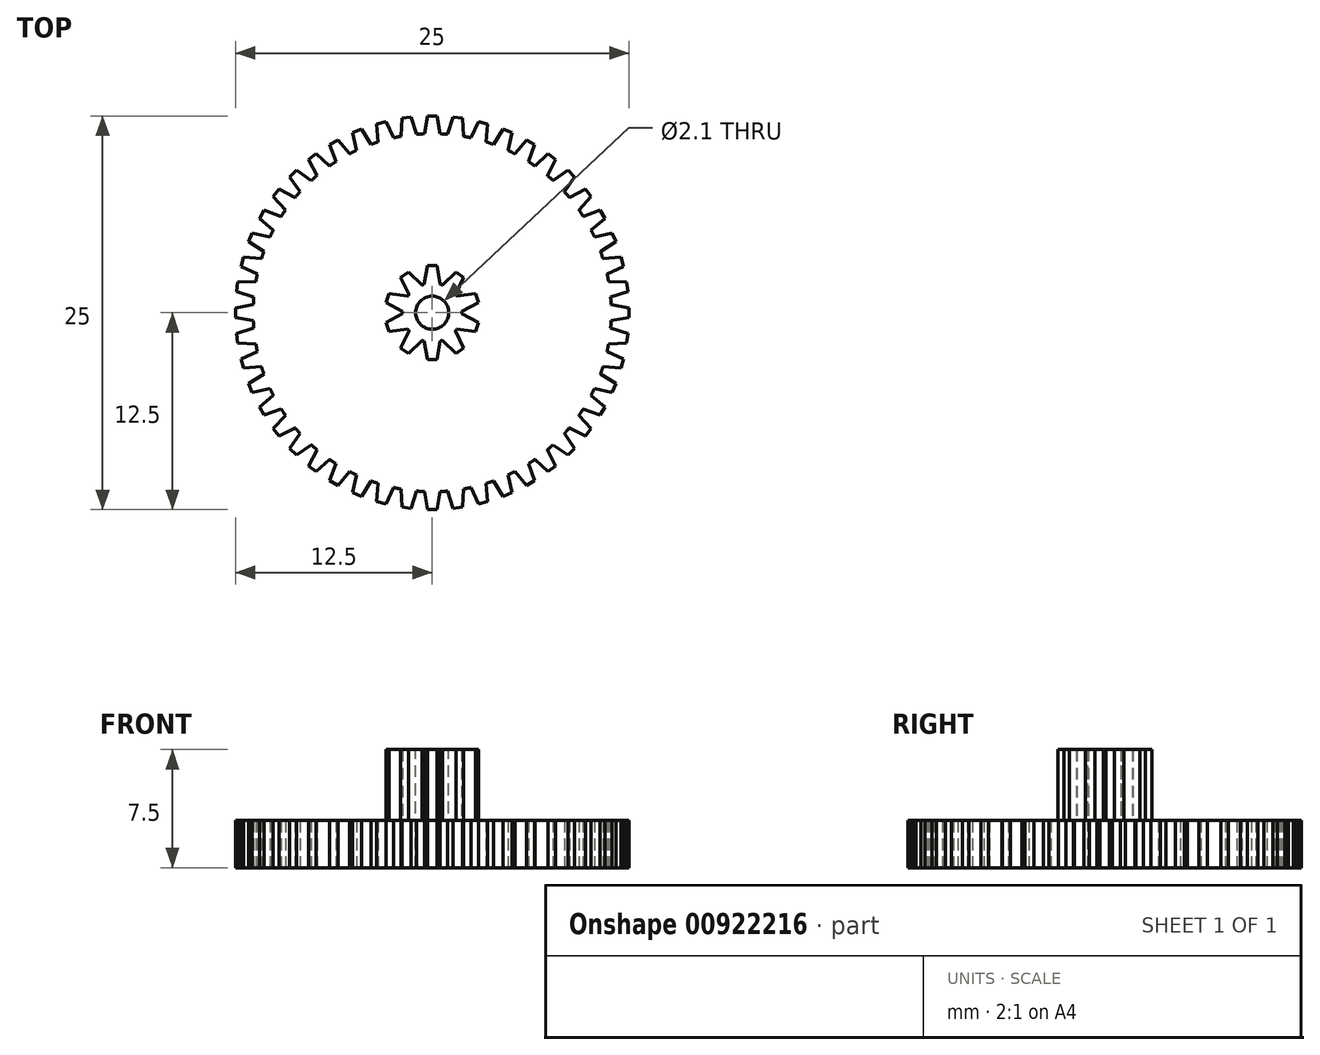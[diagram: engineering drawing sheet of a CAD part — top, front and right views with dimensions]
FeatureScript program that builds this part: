
annotation { "Feature Type Name" : "Feature", "Feature Type Description" : "" }
export const myFeature = defineFeature(function(context is Context, id is Id, definition is map)
    precondition{}
    {
        {
            var Q0;
            Q0=qCreatedBy(makeId("Top.planeOp"),FACE);
            var sketch = newSketch(context, id + "F0", { "sketchPlane" : qUnion([Q0])});
            skCircle(sketch, "E0", {"center": v(0, 0) * mm, "radius": 12 * mm, "construction": true});
            skCircle(sketch, "E1", {"center": v(0, 0) * mm, "radius": 12.5 * mm, "construction": true});
            skCircle(sketch, "E2", {"center": v(0, 0) * mm, "radius": 11.38 * mm});
            skLineSegment(sketch, "E3", {"start": v(0, 11.38) * mm, "end": v(0.5, 11.38) * mm, "construction": true});
            skLineSegment(sketch, "E4", {"start": v(0, 11.38) * mm, "end": v(-0.5, 11.38) * mm, "construction": true});
            skLineSegment(sketch, "E5", {"start": v(-1.28, 6.98) * mm, "end": v(-0.5, 11.36) * mm, "construction": true});
            skLineSegment(sketch, "E6", {"start": v(1.27, 6.98) * mm, "end": v(0.3, 12.5) * mm, "construction": true});
            skLineSegment(sketch, "E7", {"start": v(-1.27, 6.99) * mm, "end": v(-0.3, 12.5) * mm});
            skLineSegment(sketch, "E8", {"start": v(0.3, 12.5) * mm, "end": v(-0.3, 12.5) * mm});
            skLineSegment(sketch, "E9", {"start": v(0.3, 12.5) * mm, "end": v(0.5, 11.36) * mm});
            skLineSegment(sketch, "E10.1.0", {"start": v(-2.17, 6.76) * mm, "end": v(-1.93, 12.35) * mm});
            skLineSegment(sketch, "E10.1.1", {"start": v(-1.33, 12.43) * mm, "end": v(-1.93, 12.35) * mm});
            skLineSegment(sketch, "E10.1.2", {"start": v(-1.33, 12.43) * mm, "end": v(-0.99, 11.33) * mm});
            skLineSegment(sketch, "E10.2.0", {"start": v(-3.04, 6.42) * mm, "end": v(-3.53, 12) * mm});
            skLineSegment(sketch, "E10.2.1", {"start": v(-2.94, 12.15) * mm, "end": v(-3.53, 12) * mm});
            skLineSegment(sketch, "E10.2.2", {"start": v(-2.94, 12.15) * mm, "end": v(-2.46, 11.1) * mm});
            skLineSegment(sketch, "E11.1.3.0", {"start": v(-3.85, 5.97) * mm, "end": v(-5.06, 11.43) * mm});
            skLineSegment(sketch, "E11.3.3.0", {"start": v(-4.5, 11.66) * mm, "end": v(-5.06, 11.43) * mm});
            skLineSegment(sketch, "E11.6.3.0", {"start": v(-4.5, 11.66) * mm, "end": v(-3.89, 10.7) * mm});
            skLineSegment(sketch, "E11.1.4.0", {"start": v(-4.6, 5.42) * mm, "end": v(-6.5, 10.67) * mm});
            skLineSegment(sketch, "E11.3.4.0", {"start": v(-5.99, 10.97) * mm, "end": v(-6.5, 10.67) * mm});
            skLineSegment(sketch, "E11.6.4.0", {"start": v(-5.99, 10.97) * mm, "end": v(-5.25, 10.1) * mm});
            skLineSegment(sketch, "E11.1.5.0", {"start": v(-5.26, 4.77) * mm, "end": v(-7.85, 9.73) * mm});
            skLineSegment(sketch, "E11.3.5.0", {"start": v(-7.37, 10.1) * mm, "end": v(-7.85, 9.73) * mm});
            skLineSegment(sketch, "E11.6.5.0", {"start": v(-7.37, 10.1) * mm, "end": v(-6.52, 9.32) * mm});
            skLineSegment(sketch, "E11.1.6.0", {"start": v(-5.84, 4.04) * mm, "end": v(-9.05, 8.62) * mm});
            skLineSegment(sketch, "E11.3.6.0", {"start": v(-8.62, 9.05) * mm, "end": v(-9.05, 8.62) * mm});
            skLineSegment(sketch, "E11.6.6.0", {"start": v(-8.62, 9.05) * mm, "end": v(-7.68, 8.4) * mm});
            skLineSegment(sketch, "E11.1.7.0", {"start": v(-6.32, 3.24) * mm, "end": v(-10.1, 7.37) * mm});
            skLineSegment(sketch, "E11.3.7.0", {"start": v(-9.73, 7.85) * mm, "end": v(-10.1, 7.37) * mm});
            skLineSegment(sketch, "E11.6.7.0", {"start": v(-9.73, 7.85) * mm, "end": v(-8.71, 7.32) * mm});
            skLineSegment(sketch, "E11.1.8.0", {"start": v(-6.69, 2.4) * mm, "end": v(-10.97, 5.99) * mm});
            skLineSegment(sketch, "E11.3.8.0", {"start": v(-10.67, 6.5) * mm, "end": v(-10.97, 5.99) * mm});
            skLineSegment(sketch, "E11.6.8.0", {"start": v(-10.67, 6.5) * mm, "end": v(-9.6, 6.12) * mm});
            skLineSegment(sketch, "E11.1.9.0", {"start": v(-6.94, 1.5) * mm, "end": v(-11.66, 4.5) * mm});
            skLineSegment(sketch, "E11.3.9.0", {"start": v(-11.43, 5.06) * mm, "end": v(-11.66, 4.5) * mm});
            skLineSegment(sketch, "E11.6.9.0", {"start": v(-11.43, 5.06) * mm, "end": v(-10.3, 4.81) * mm});
            skLineSegment(sketch, "E11.1.10.0", {"start": v(-7.08, 0.58) * mm, "end": v(-12.15, 2.94) * mm});
            skLineSegment(sketch, "E11.3.10.0", {"start": v(-12, 3.53) * mm, "end": v(-12.15, 2.94) * mm});
            skLineSegment(sketch, "E11.6.10.0", {"start": v(-12, 3.53) * mm, "end": v(-10.85, 3.43) * mm});
            skLineSegment(sketch, "E11.1.11.0", {"start": v(-7.1, -0.35) * mm, "end": v(-12.43, 1.33) * mm});
            skLineSegment(sketch, "E11.3.11.0", {"start": v(-12.35, 1.93) * mm, "end": v(-12.43, 1.33) * mm});
            skLineSegment(sketch, "E11.6.11.0", {"start": v(-12.35, 1.93) * mm, "end": v(-11.2, 1.98) * mm});
            skLineSegment(sketch, "E11.1.12.0", {"start": v(-6.99, -1.27) * mm, "end": v(-12.5, -0.3) * mm});
            skLineSegment(sketch, "E11.3.12.0", {"start": v(-12.5, 0.3) * mm, "end": v(-12.5, -0.3) * mm});
            skLineSegment(sketch, "E11.6.12.0", {"start": v(-12.5, 0.3) * mm, "end": v(-11.36, 0.5) * mm});
            skLineSegment(sketch, "E11.1.13.0", {"start": v(-6.76, -2.17) * mm, "end": v(-12.35, -1.93) * mm});
            skLineSegment(sketch, "E11.3.13.0", {"start": v(-12.43, -1.33) * mm, "end": v(-12.35, -1.93) * mm});
            skLineSegment(sketch, "E11.6.13.0", {"start": v(-12.43, -1.33) * mm, "end": v(-11.33, -0.99) * mm});
            skLineSegment(sketch, "E11.1.14.0", {"start": v(-6.42, -3.04) * mm, "end": v(-12, -3.53) * mm});
            skLineSegment(sketch, "E11.3.14.0", {"start": v(-12.15, -2.94) * mm, "end": v(-12, -3.53) * mm});
            skLineSegment(sketch, "E11.6.14.0", {"start": v(-12.15, -2.94) * mm, "end": v(-11.1, -2.46) * mm});
            skLineSegment(sketch, "E11.1.15.0", {"start": v(-5.97, -3.85) * mm, "end": v(-11.43, -5.06) * mm});
            skLineSegment(sketch, "E11.3.15.0", {"start": v(-11.66, -4.5) * mm, "end": v(-11.43, -5.06) * mm});
            skLineSegment(sketch, "E11.6.15.0", {"start": v(-11.66, -4.5) * mm, "end": v(-10.7, -3.89) * mm});
            skLineSegment(sketch, "E11.1.16.0", {"start": v(-5.42, -4.6) * mm, "end": v(-10.67, -6.5) * mm});
            skLineSegment(sketch, "E11.3.16.0", {"start": v(-10.97, -5.99) * mm, "end": v(-10.67, -6.5) * mm});
            skLineSegment(sketch, "E11.6.16.0", {"start": v(-10.97, -5.99) * mm, "end": v(-10.1, -5.25) * mm});
            skLineSegment(sketch, "E11.1.17.0", {"start": v(-4.77, -5.26) * mm, "end": v(-9.73, -7.85) * mm});
            skLineSegment(sketch, "E11.3.17.0", {"start": v(-10.1, -7.37) * mm, "end": v(-9.73, -7.85) * mm});
            skLineSegment(sketch, "E11.6.17.0", {"start": v(-10.1, -7.37) * mm, "end": v(-9.32, -6.52) * mm});
            skLineSegment(sketch, "E11.1.18.0", {"start": v(-4.04, -5.84) * mm, "end": v(-8.62, -9.05) * mm});
            skLineSegment(sketch, "E11.3.18.0", {"start": v(-9.05, -8.62) * mm, "end": v(-8.62, -9.05) * mm});
            skLineSegment(sketch, "E11.6.18.0", {"start": v(-9.05, -8.62) * mm, "end": v(-8.4, -7.68) * mm});
            skLineSegment(sketch, "E11.1.19.0", {"start": v(-3.24, -6.32) * mm, "end": v(-7.37, -10.1) * mm});
            skLineSegment(sketch, "E11.3.19.0", {"start": v(-7.85, -9.73) * mm, "end": v(-7.37, -10.1) * mm});
            skLineSegment(sketch, "E11.6.19.0", {"start": v(-7.85, -9.73) * mm, "end": v(-7.32, -8.71) * mm});
            skLineSegment(sketch, "E11.1.20.0", {"start": v(-2.4, -6.69) * mm, "end": v(-5.99, -10.97) * mm});
            skLineSegment(sketch, "E11.3.20.0", {"start": v(-6.5, -10.67) * mm, "end": v(-5.99, -10.97) * mm});
            skLineSegment(sketch, "E11.6.20.0", {"start": v(-6.5, -10.67) * mm, "end": v(-6.12, -9.6) * mm});
            skLineSegment(sketch, "E11.1.21.0", {"start": v(-1.5, -6.94) * mm, "end": v(-4.5, -11.66) * mm});
            skLineSegment(sketch, "E11.3.21.0", {"start": v(-5.06, -11.43) * mm, "end": v(-4.5, -11.66) * mm});
            skLineSegment(sketch, "E11.6.21.0", {"start": v(-5.06, -11.43) * mm, "end": v(-4.81, -10.3) * mm});
            skLineSegment(sketch, "E11.1.22.0", {"start": v(-0.58, -7.08) * mm, "end": v(-2.94, -12.15) * mm});
            skLineSegment(sketch, "E11.3.22.0", {"start": v(-3.53, -12) * mm, "end": v(-2.94, -12.15) * mm});
            skLineSegment(sketch, "E11.6.22.0", {"start": v(-3.53, -12) * mm, "end": v(-3.43, -10.85) * mm});
            skLineSegment(sketch, "E11.1.23.0", {"start": v(0.35, -7.1) * mm, "end": v(-1.33, -12.43) * mm});
            skLineSegment(sketch, "E11.3.23.0", {"start": v(-1.93, -12.35) * mm, "end": v(-1.33, -12.43) * mm});
            skLineSegment(sketch, "E11.6.23.0", {"start": v(-1.93, -12.35) * mm, "end": v(-1.98, -11.2) * mm});
            skLineSegment(sketch, "E11.1.24.0", {"start": v(1.27, -6.99) * mm, "end": v(0.3, -12.5) * mm});
            skLineSegment(sketch, "E11.3.24.0", {"start": v(-0.3, -12.5) * mm, "end": v(0.3, -12.5) * mm});
            skLineSegment(sketch, "E11.6.24.0", {"start": v(-0.3, -12.5) * mm, "end": v(-0.5, -11.36) * mm});
            skLineSegment(sketch, "E11.1.25.0", {"start": v(2.17, -6.76) * mm, "end": v(1.93, -12.35) * mm});
            skLineSegment(sketch, "E11.3.25.0", {"start": v(1.33, -12.43) * mm, "end": v(1.93, -12.35) * mm});
            skLineSegment(sketch, "E11.6.25.0", {"start": v(1.33, -12.43) * mm, "end": v(0.99, -11.33) * mm});
            skLineSegment(sketch, "E11.1.26.0", {"start": v(3.04, -6.42) * mm, "end": v(3.53, -12) * mm});
            skLineSegment(sketch, "E11.3.26.0", {"start": v(2.94, -12.15) * mm, "end": v(3.53, -12) * mm});
            skLineSegment(sketch, "E11.6.26.0", {"start": v(2.94, -12.15) * mm, "end": v(2.46, -11.1) * mm});
            skLineSegment(sketch, "E11.1.27.0", {"start": v(3.85, -5.97) * mm, "end": v(5.06, -11.43) * mm});
            skLineSegment(sketch, "E11.3.27.0", {"start": v(4.5, -11.66) * mm, "end": v(5.06, -11.43) * mm});
            skLineSegment(sketch, "E11.6.27.0", {"start": v(4.5, -11.66) * mm, "end": v(3.89, -10.7) * mm});
            skLineSegment(sketch, "E11.1.28.0", {"start": v(4.6, -5.42) * mm, "end": v(6.5, -10.67) * mm});
            skLineSegment(sketch, "E11.3.28.0", {"start": v(5.99, -10.97) * mm, "end": v(6.5, -10.67) * mm});
            skLineSegment(sketch, "E11.6.28.0", {"start": v(5.99, -10.97) * mm, "end": v(5.25, -10.1) * mm});
            skLineSegment(sketch, "E11.1.29.0", {"start": v(5.26, -4.77) * mm, "end": v(7.85, -9.73) * mm});
            skLineSegment(sketch, "E11.3.29.0", {"start": v(7.37, -10.1) * mm, "end": v(7.85, -9.73) * mm});
            skLineSegment(sketch, "E11.6.29.0", {"start": v(7.37, -10.1) * mm, "end": v(6.52, -9.32) * mm});
            skLineSegment(sketch, "E12.1.30.0", {"start": v(5.84, -4.04) * mm, "end": v(9.05, -8.62) * mm});
            skLineSegment(sketch, "E12.3.30.0", {"start": v(8.62, -9.05) * mm, "end": v(9.05, -8.62) * mm});
            skLineSegment(sketch, "E12.6.30.0", {"start": v(8.62, -9.05) * mm, "end": v(7.68, -8.4) * mm});
            skLineSegment(sketch, "E12.1.31.0", {"start": v(6.32, -3.24) * mm, "end": v(10.1, -7.37) * mm});
            skLineSegment(sketch, "E12.3.31.0", {"start": v(9.73, -7.85) * mm, "end": v(10.1, -7.37) * mm});
            skLineSegment(sketch, "E12.6.31.0", {"start": v(9.73, -7.85) * mm, "end": v(8.71, -7.32) * mm});
            skLineSegment(sketch, "E12.1.32.0", {"start": v(6.69, -2.4) * mm, "end": v(10.97, -5.99) * mm});
            skLineSegment(sketch, "E12.3.32.0", {"start": v(10.67, -6.5) * mm, "end": v(10.97, -5.99) * mm});
            skLineSegment(sketch, "E12.6.32.0", {"start": v(10.67, -6.5) * mm, "end": v(9.6, -6.12) * mm});
            skLineSegment(sketch, "E12.1.33.0", {"start": v(6.94, -1.5) * mm, "end": v(11.66, -4.5) * mm});
            skLineSegment(sketch, "E12.3.33.0", {"start": v(11.43, -5.06) * mm, "end": v(11.66, -4.5) * mm});
            skLineSegment(sketch, "E12.6.33.0", {"start": v(11.43, -5.06) * mm, "end": v(10.3, -4.81) * mm});
            skLineSegment(sketch, "E12.1.34.0", {"start": v(7.08, -0.58) * mm, "end": v(12.15, -2.94) * mm});
            skLineSegment(sketch, "E12.3.34.0", {"start": v(12, -3.53) * mm, "end": v(12.15, -2.94) * mm});
            skLineSegment(sketch, "E12.6.34.0", {"start": v(12, -3.53) * mm, "end": v(10.85, -3.43) * mm});
            skLineSegment(sketch, "E12.1.35.0", {"start": v(7.1, 0.35) * mm, "end": v(12.43, -1.33) * mm});
            skLineSegment(sketch, "E12.3.35.0", {"start": v(12.35, -1.93) * mm, "end": v(12.43, -1.33) * mm});
            skLineSegment(sketch, "E12.6.35.0", {"start": v(12.35, -1.93) * mm, "end": v(11.2, -1.98) * mm});
            skLineSegment(sketch, "E12.1.36.0", {"start": v(6.99, 1.27) * mm, "end": v(12.5, 0.3) * mm});
            skLineSegment(sketch, "E12.3.36.0", {"start": v(12.5, -0.3) * mm, "end": v(12.5, 0.3) * mm});
            skLineSegment(sketch, "E12.6.36.0", {"start": v(12.5, -0.3) * mm, "end": v(11.36, -0.5) * mm});
            skLineSegment(sketch, "E12.1.37.0", {"start": v(6.76, 2.17) * mm, "end": v(12.35, 1.93) * mm});
            skLineSegment(sketch, "E12.3.37.0", {"start": v(12.43, 1.33) * mm, "end": v(12.35, 1.93) * mm});
            skLineSegment(sketch, "E12.6.37.0", {"start": v(12.43, 1.33) * mm, "end": v(11.33, 0.99) * mm});
            skLineSegment(sketch, "E12.1.38.0", {"start": v(6.42, 3.04) * mm, "end": v(12, 3.53) * mm});
            skLineSegment(sketch, "E12.3.38.0", {"start": v(12.15, 2.94) * mm, "end": v(12, 3.53) * mm});
            skLineSegment(sketch, "E12.6.38.0", {"start": v(12.15, 2.94) * mm, "end": v(11.1, 2.46) * mm});
            skLineSegment(sketch, "E12.1.39.0", {"start": v(5.97, 3.85) * mm, "end": v(11.43, 5.06) * mm});
            skLineSegment(sketch, "E12.3.39.0", {"start": v(11.66, 4.5) * mm, "end": v(11.43, 5.06) * mm});
            skLineSegment(sketch, "E12.6.39.0", {"start": v(11.66, 4.5) * mm, "end": v(10.7, 3.89) * mm});
            skLineSegment(sketch, "E12.1.40.0", {"start": v(5.42, 4.6) * mm, "end": v(10.67, 6.5) * mm});
            skLineSegment(sketch, "E12.3.40.0", {"start": v(10.97, 5.99) * mm, "end": v(10.67, 6.5) * mm});
            skLineSegment(sketch, "E12.6.40.0", {"start": v(10.97, 5.99) * mm, "end": v(10.1, 5.25) * mm});
            skLineSegment(sketch, "E12.1.41.0", {"start": v(4.77, 5.26) * mm, "end": v(9.73, 7.85) * mm});
            skLineSegment(sketch, "E12.3.41.0", {"start": v(10.1, 7.37) * mm, "end": v(9.73, 7.85) * mm});
            skLineSegment(sketch, "E12.6.41.0", {"start": v(10.1, 7.37) * mm, "end": v(9.32, 6.52) * mm});
            skLineSegment(sketch, "E13.1.42.0", {"start": v(4.04, 5.84) * mm, "end": v(8.62, 9.05) * mm});
            skLineSegment(sketch, "E13.3.42.0", {"start": v(9.05, 8.62) * mm, "end": v(8.62, 9.05) * mm});
            skLineSegment(sketch, "E13.6.42.0", {"start": v(9.05, 8.62) * mm, "end": v(8.4, 7.68) * mm});
            skLineSegment(sketch, "E13.1.43.0", {"start": v(3.24, 6.32) * mm, "end": v(7.37, 10.1) * mm});
            skLineSegment(sketch, "E13.3.43.0", {"start": v(7.85, 9.73) * mm, "end": v(7.37, 10.1) * mm});
            skLineSegment(sketch, "E13.6.43.0", {"start": v(7.85, 9.73) * mm, "end": v(7.32, 8.71) * mm});
            skLineSegment(sketch, "E13.1.44.0", {"start": v(2.4, 6.69) * mm, "end": v(5.99, 10.97) * mm});
            skLineSegment(sketch, "E13.3.44.0", {"start": v(6.5, 10.67) * mm, "end": v(5.99, 10.97) * mm});
            skLineSegment(sketch, "E13.6.44.0", {"start": v(6.5, 10.67) * mm, "end": v(6.12, 9.6) * mm});
            skLineSegment(sketch, "E13.1.45.0", {"start": v(1.5, 6.94) * mm, "end": v(4.5, 11.66) * mm});
            skLineSegment(sketch, "E13.3.45.0", {"start": v(5.06, 11.43) * mm, "end": v(4.5, 11.66) * mm});
            skLineSegment(sketch, "E13.6.45.0", {"start": v(5.06, 11.43) * mm, "end": v(4.81, 10.3) * mm});
            skLineSegment(sketch, "E13.1.46.0", {"start": v(0.58, 7.08) * mm, "end": v(2.94, 12.15) * mm});
            skLineSegment(sketch, "E13.3.46.0", {"start": v(3.53, 12) * mm, "end": v(2.94, 12.15) * mm});
            skLineSegment(sketch, "E13.6.46.0", {"start": v(3.53, 12) * mm, "end": v(3.43, 10.85) * mm});
            skLineSegment(sketch, "E13.1.47.0", {"start": v(-0.35, 7.1) * mm, "end": v(1.33, 12.43) * mm});
            skLineSegment(sketch, "E13.3.47.0", {"start": v(1.93, 12.35) * mm, "end": v(1.33, 12.43) * mm});
            skLineSegment(sketch, "E13.6.47.0", {"start": v(1.93, 12.35) * mm, "end": v(1.98, 11.2) * mm});
            skSolve(sketch);
        }
        {
            var Q0;
            Q0=qSketchRegion(id+"F0",true);
            extrude(context, id + "F1", {"entities" : qUnion([Q0]), "depth" : 3 * mm, "offsetDistance" : 25 * mm});
        }
        {
            var Q0;
            Q0=makeQuery(id+"F1.opExtrude","CAP_FACE",FACE,{"disambiguationData":[OSD([sQuery(id+"F0.wireOp",EDGE,"E2"),sQuery(id+"F0.wireOp",EDGE,"E7"),sQuery(id+"F0.wireOp",EDGE,"E8"),sQuery(id+"F0.wireOp",EDGE,"E9"),sQuery(id+"F0.wireOp",EDGE,"E10.1.0"),sQuery(id+"F0.wireOp",EDGE,"E10.1.1"),sQuery(id+"F0.wireOp",EDGE,"E10.1.2"),sQuery(id+"F0.wireOp",EDGE,"E10.2.0"),sQuery(id+"F0.wireOp",EDGE,"E10.2.1"),sQuery(id+"F0.wireOp",EDGE,"E10.2.2"),sQuery(id+"F0.wireOp",EDGE,"E11.1.3.0"),sQuery(id+"F0.wireOp",EDGE,"E11.3.3.0"),sQuery(id+"F0.wireOp",EDGE,"E11.6.3.0"),sQuery(id+"F0.wireOp",EDGE,"E11.1.4.0"),sQuery(id+"F0.wireOp",EDGE,"E11.3.4.0"),sQuery(id+"F0.wireOp",EDGE,"E11.6.4.0"),sQuery(id+"F0.wireOp",EDGE,"E11.1.5.0"),sQuery(id+"F0.wireOp",EDGE,"E11.3.5.0"),sQuery(id+"F0.wireOp",EDGE,"E11.6.5.0"),sQuery(id+"F0.wireOp",EDGE,"E11.1.6.0"),sQuery(id+"F0.wireOp",EDGE,"E11.3.6.0"),sQuery(id+"F0.wireOp",EDGE,"E11.6.6.0"),sQuery(id+"F0.wireOp",EDGE,"E11.1.7.0"),sQuery(id+"F0.wireOp",EDGE,"E11.3.7.0"),sQuery(id+"F0.wireOp",EDGE,"E11.6.7.0"),sQuery(id+"F0.wireOp",EDGE,"E11.1.8.0"),sQuery(id+"F0.wireOp",EDGE,"E11.3.8.0"),sQuery(id+"F0.wireOp",EDGE,"E11.6.8.0"),sQuery(id+"F0.wireOp",EDGE,"E11.1.9.0"),sQuery(id+"F0.wireOp",EDGE,"E11.3.9.0"),sQuery(id+"F0.wireOp",EDGE,"E11.6.9.0"),sQuery(id+"F0.wireOp",EDGE,"E11.1.10.0"),sQuery(id+"F0.wireOp",EDGE,"E11.3.10.0"),sQuery(id+"F0.wireOp",EDGE,"E11.6.10.0"),sQuery(id+"F0.wireOp",EDGE,"E11.1.11.0"),sQuery(id+"F0.wireOp",EDGE,"E11.3.11.0"),sQuery(id+"F0.wireOp",EDGE,"E11.6.11.0"),sQuery(id+"F0.wireOp",EDGE,"E11.1.12.0"),sQuery(id+"F0.wireOp",EDGE,"E11.3.12.0"),sQuery(id+"F0.wireOp",EDGE,"E11.6.12.0"),sQuery(id+"F0.wireOp",EDGE,"E11.1.13.0"),sQuery(id+"F0.wireOp",EDGE,"E11.3.13.0"),sQuery(id+"F0.wireOp",EDGE,"E11.6.13.0"),sQuery(id+"F0.wireOp",EDGE,"E11.1.14.0"),sQuery(id+"F0.wireOp",EDGE,"E11.3.14.0"),sQuery(id+"F0.wireOp",EDGE,"E11.6.14.0"),sQuery(id+"F0.wireOp",EDGE,"E11.1.15.0"),sQuery(id+"F0.wireOp",EDGE,"E11.3.15.0"),sQuery(id+"F0.wireOp",EDGE,"E11.6.15.0"),sQuery(id+"F0.wireOp",EDGE,"E11.1.16.0"),sQuery(id+"F0.wireOp",EDGE,"E11.3.16.0"),sQuery(id+"F0.wireOp",EDGE,"E11.6.16.0"),sQuery(id+"F0.wireOp",EDGE,"E11.1.17.0"),sQuery(id+"F0.wireOp",EDGE,"E11.3.17.0"),sQuery(id+"F0.wireOp",EDGE,"E11.6.17.0"),sQuery(id+"F0.wireOp",EDGE,"E11.1.18.0"),sQuery(id+"F0.wireOp",EDGE,"E11.3.18.0"),sQuery(id+"F0.wireOp",EDGE,"E11.6.18.0"),sQuery(id+"F0.wireOp",EDGE,"E11.1.19.0"),sQuery(id+"F0.wireOp",EDGE,"E11.3.19.0"),sQuery(id+"F0.wireOp",EDGE,"E11.6.19.0"),sQuery(id+"F0.wireOp",EDGE,"E11.1.20.0"),sQuery(id+"F0.wireOp",EDGE,"E11.3.20.0"),sQuery(id+"F0.wireOp",EDGE,"E11.6.20.0"),sQuery(id+"F0.wireOp",EDGE,"E11.1.21.0"),sQuery(id+"F0.wireOp",EDGE,"E11.3.21.0"),sQuery(id+"F0.wireOp",EDGE,"E11.6.21.0"),sQuery(id+"F0.wireOp",EDGE,"E11.1.22.0"),sQuery(id+"F0.wireOp",EDGE,"E11.3.22.0"),sQuery(id+"F0.wireOp",EDGE,"E11.6.22.0"),sQuery(id+"F0.wireOp",EDGE,"E11.1.23.0"),sQuery(id+"F0.wireOp",EDGE,"E11.3.23.0"),sQuery(id+"F0.wireOp",EDGE,"E11.6.23.0"),sQuery(id+"F0.wireOp",EDGE,"E11.1.24.0"),sQuery(id+"F0.wireOp",EDGE,"E11.3.24.0"),sQuery(id+"F0.wireOp",EDGE,"E11.6.24.0"),sQuery(id+"F0.wireOp",EDGE,"E11.1.25.0"),sQuery(id+"F0.wireOp",EDGE,"E11.3.25.0"),sQuery(id+"F0.wireOp",EDGE,"E11.6.25.0"),sQuery(id+"F0.wireOp",EDGE,"E11.1.26.0"),sQuery(id+"F0.wireOp",EDGE,"E11.3.26.0"),sQuery(id+"F0.wireOp",EDGE,"E11.6.26.0"),sQuery(id+"F0.wireOp",EDGE,"E11.1.27.0"),sQuery(id+"F0.wireOp",EDGE,"E11.3.27.0"),sQuery(id+"F0.wireOp",EDGE,"E11.6.27.0"),sQuery(id+"F0.wireOp",EDGE,"E11.1.28.0"),sQuery(id+"F0.wireOp",EDGE,"E11.3.28.0"),sQuery(id+"F0.wireOp",EDGE,"E11.6.28.0"),sQuery(id+"F0.wireOp",EDGE,"E11.1.29.0"),sQuery(id+"F0.wireOp",EDGE,"E11.3.29.0"),sQuery(id+"F0.wireOp",EDGE,"E11.6.29.0")])],"isStart":false});
            var sketch = newSketch(context, id + "F2", { "sketchPlane" : qUnion([Q0])});
            skCircle(sketch, "E14", {"center": v(0, 0) * mm, "radius": 2.5 * mm, "construction": true});
            skCircle(sketch, "E15", {"center": v(0, 0) * mm, "radius": 3 * mm, "construction": true});
            skCircle(sketch, "E16", {"center": v(0, 0) * mm, "radius": 1.88 * mm});
            skLineSegment(sketch, "E17", {"start": v(0, 1.88) * mm, "end": v(0.5, 1.88) * mm, "construction": true});
            skLineSegment(sketch, "E18", {"start": v(0, 1.88) * mm, "end": v(-0.5, 1.88) * mm, "construction": true});
            skLineSegment(sketch, "E19", {"start": v(-0.51, 1.8) * mm, "end": v(-0.3, 2.98) * mm, "construction": true});
            skLineSegment(sketch, "E20", {"start": v(0.51, 1.8) * mm, "end": v(0.3, 2.98) * mm, "construction": true});
            skLineSegment(sketch, "E21", {"start": v(-0.51, 1.8) * mm, "end": v(-0.3, 2.98) * mm});
            skLineSegment(sketch, "E22", {"start": v(0.3, 2.98) * mm, "end": v(-0.3, 2.98) * mm});
            skLineSegment(sketch, "E23", {"start": v(0.3, 2.98) * mm, "end": v(0.51, 1.8) * mm});
            skLineSegment(sketch, "E24.1.0", {"start": v(-1.47, 1.16) * mm, "end": v(-2, 2.24) * mm});
            skLineSegment(sketch, "E24.1.1", {"start": v(-1.5, 2.6) * mm, "end": v(-2, 2.24) * mm});
            skLineSegment(sketch, "E24.1.2", {"start": v(-1.5, 2.6) * mm, "end": v(-0.65, 1.76) * mm});
            skLineSegment(sketch, "E24.2.0", {"start": v(-1.87, 0.07) * mm, "end": v(-2.93, 0.63) * mm});
            skLineSegment(sketch, "E24.2.1", {"start": v(-2.74, 1.21) * mm, "end": v(-2.93, 0.63) * mm});
            skLineSegment(sketch, "E24.2.2", {"start": v(-2.74, 1.21) * mm, "end": v(-1.56, 1.04) * mm});
            skLineSegment(sketch, "E25.1.3.0", {"start": v(-1.56, -1.04) * mm, "end": v(-2.74, -1.21) * mm});
            skLineSegment(sketch, "E25.3.3.0", {"start": v(-2.93, -0.63) * mm, "end": v(-2.74, -1.21) * mm});
            skLineSegment(sketch, "E25.6.3.0", {"start": v(-2.93, -0.63) * mm, "end": v(-1.87, -0.07) * mm});
            skLineSegment(sketch, "E25.1.4.0", {"start": v(-0.65, -1.76) * mm, "end": v(-1.5, -2.6) * mm});
            skLineSegment(sketch, "E25.3.4.0", {"start": v(-2, -2.24) * mm, "end": v(-1.5, -2.6) * mm});
            skLineSegment(sketch, "E25.6.4.0", {"start": v(-2, -2.24) * mm, "end": v(-1.47, -1.16) * mm});
            skLineSegment(sketch, "E25.1.5.0", {"start": v(0.51, -1.8) * mm, "end": v(0.3, -2.98) * mm});
            skLineSegment(sketch, "E25.3.5.0", {"start": v(-0.3, -2.98) * mm, "end": v(0.3, -2.98) * mm});
            skLineSegment(sketch, "E25.6.5.0", {"start": v(-0.3, -2.98) * mm, "end": v(-0.51, -1.8) * mm});
            skLineSegment(sketch, "E25.1.6.0", {"start": v(1.47, -1.16) * mm, "end": v(2, -2.24) * mm});
            skLineSegment(sketch, "E25.3.6.0", {"start": v(1.5, -2.6) * mm, "end": v(2, -2.24) * mm});
            skLineSegment(sketch, "E25.6.6.0", {"start": v(1.5, -2.6) * mm, "end": v(0.65, -1.76) * mm});
            skLineSegment(sketch, "E25.1.7.0", {"start": v(1.87, -0.07) * mm, "end": v(2.93, -0.63) * mm});
            skLineSegment(sketch, "E25.3.7.0", {"start": v(2.74, -1.21) * mm, "end": v(2.93, -0.63) * mm});
            skLineSegment(sketch, "E25.6.7.0", {"start": v(2.74, -1.21) * mm, "end": v(1.56, -1.04) * mm});
            skLineSegment(sketch, "E25.1.8.0", {"start": v(1.56, 1.04) * mm, "end": v(2.74, 1.21) * mm});
            skLineSegment(sketch, "E25.3.8.0", {"start": v(2.93, 0.63) * mm, "end": v(2.74, 1.21) * mm});
            skLineSegment(sketch, "E25.6.8.0", {"start": v(2.93, 0.63) * mm, "end": v(1.87, 0.07) * mm});
            skLineSegment(sketch, "E25.1.9.0", {"start": v(0.65, 1.76) * mm, "end": v(1.5, 2.6) * mm});
            skLineSegment(sketch, "E25.3.9.0", {"start": v(2, 2.24) * mm, "end": v(1.5, 2.6) * mm});
            skLineSegment(sketch, "E25.6.9.0", {"start": v(2, 2.24) * mm, "end": v(1.47, 1.16) * mm});
            skSolve(sketch);
        }
        {
            var Q0;
            Q0=qSketchRegion(id+"F2",true);
            extrude(context, id + "F3", {"entities" : qUnion([Q0]), "operationType" : NewBodyOperationType.ADD, "depth" : 4.5 * mm, "offsetDistance" : 25 * mm});
        }
        {
            var Q0;
            Q0=makeQuery(id+"F3.opExtrude","CAP_FACE",FACE,{"disambiguationData":[OSD([sQuery(id+"F2.wireOp",EDGE,"E16"),sQuery(id+"F2.wireOp",EDGE,"E21"),sQuery(id+"F2.wireOp",EDGE,"E22"),sQuery(id+"F2.wireOp",EDGE,"E23"),sQuery(id+"F2.wireOp",EDGE,"E24.1.0"),sQuery(id+"F2.wireOp",EDGE,"E24.1.1"),sQuery(id+"F2.wireOp",EDGE,"E24.1.2"),sQuery(id+"F2.wireOp",EDGE,"E24.2.0"),sQuery(id+"F2.wireOp",EDGE,"E24.2.1"),sQuery(id+"F2.wireOp",EDGE,"E24.2.2"),sQuery(id+"F2.wireOp",EDGE,"E25.1.3.0"),sQuery(id+"F2.wireOp",EDGE,"E25.3.3.0"),sQuery(id+"F2.wireOp",EDGE,"E25.6.3.0"),sQuery(id+"F2.wireOp",EDGE,"E25.1.4.0"),sQuery(id+"F2.wireOp",EDGE,"E25.3.4.0"),sQuery(id+"F2.wireOp",EDGE,"E25.6.4.0"),sQuery(id+"F2.wireOp",EDGE,"E25.1.5.0"),sQuery(id+"F2.wireOp",EDGE,"E25.3.5.0"),sQuery(id+"F2.wireOp",EDGE,"E25.6.5.0"),sQuery(id+"F2.wireOp",EDGE,"E25.1.6.0"),sQuery(id+"F2.wireOp",EDGE,"E25.3.6.0"),sQuery(id+"F2.wireOp",EDGE,"E25.6.6.0"),sQuery(id+"F2.wireOp",EDGE,"E25.1.7.0"),sQuery(id+"F2.wireOp",EDGE,"E25.3.7.0"),sQuery(id+"F2.wireOp",EDGE,"E25.6.7.0"),sQuery(id+"F2.wireOp",EDGE,"E25.1.8.0"),sQuery(id+"F2.wireOp",EDGE,"E25.3.8.0"),sQuery(id+"F2.wireOp",EDGE,"E25.6.8.0"),sQuery(id+"F2.wireOp",EDGE,"E25.1.9.0"),sQuery(id+"F2.wireOp",EDGE,"E25.3.9.0"),sQuery(id+"F2.wireOp",EDGE,"E25.6.9.0")])],"isStart":false});
            var sketch = newSketch(context, id + "F4", { "sketchPlane" : qUnion([Q0])});
            skCircle(sketch, "E26", {"center": v(0, 0) * mm, "radius": 1.05 * mm});
            skSolve(sketch);
        }
        {
            var Q0;
            Q0=qSketchRegion(id+"F4",true);
            extrude(context, id + "F5", {"entities" : qUnion([Q0]), "operationType" : NewBodyOperationType.REMOVE, "endBound" : BoundingType.THROUGH_ALL, "oppositeDirection" : true, "depth" : 25 * mm, "offsetDistance" : 25 * mm});
        }
    });
